# Revit family: Haworth_Massimosistema_WideSofa_TwoArms
name_source: partatom
category: Furniture
revit_build: Autodesk Revit 2018 (Build: 20170223_1515(x64)
units: mm (PartAtom-declared; Revit-internal decimal feet)

## family parameters
Always vertical = Yes
Cut with Voids When Loaded = No
OmniClass Number = 23.40.20.00
OmniClass Title = General Furniture and Specialties
Room Calculation Point = No
Shared = No
Work Plane-Based = No

## types (2) — shared parameters
Actual Depth = 39 1/4"
Actual Height = 33 3/4"
Assembly Code = E2020200
Cushion Width = 78 3/4"
Frame Finish = Haworth _ Paint _ Metallic Gunmetal
Manufacturer = Haworth
Model = HCPF-MSS2
Size = Verify Final Dim. w/ Haworth
URL = http://www.haworth.com
URL - Product = http://www.haworth.com
Version = 1
Warranty = https://www.haworth.com

## per-type parameters (varying)
| type | Actual Width | Arm High | Arm Width | Description | High | Low | Two Seat Control |
| HCPF-MSS2-HHP | 95 3/4" | 28" | 8 1/2" | Haworth Massimosistema Sofa - Wide High Arms - Two Seats | Yes | No | Yes |
| HCPF-MSS2-LLP | 98" | 22 3/4" | 9 5/8" | Haworth Massimosistema Sofa - Wide Low Arms - Two Seats | No | Yes | No |

## geometry (parser evidence)
native form markers: Sweep x12
no freeform markers — native parametric forms only
